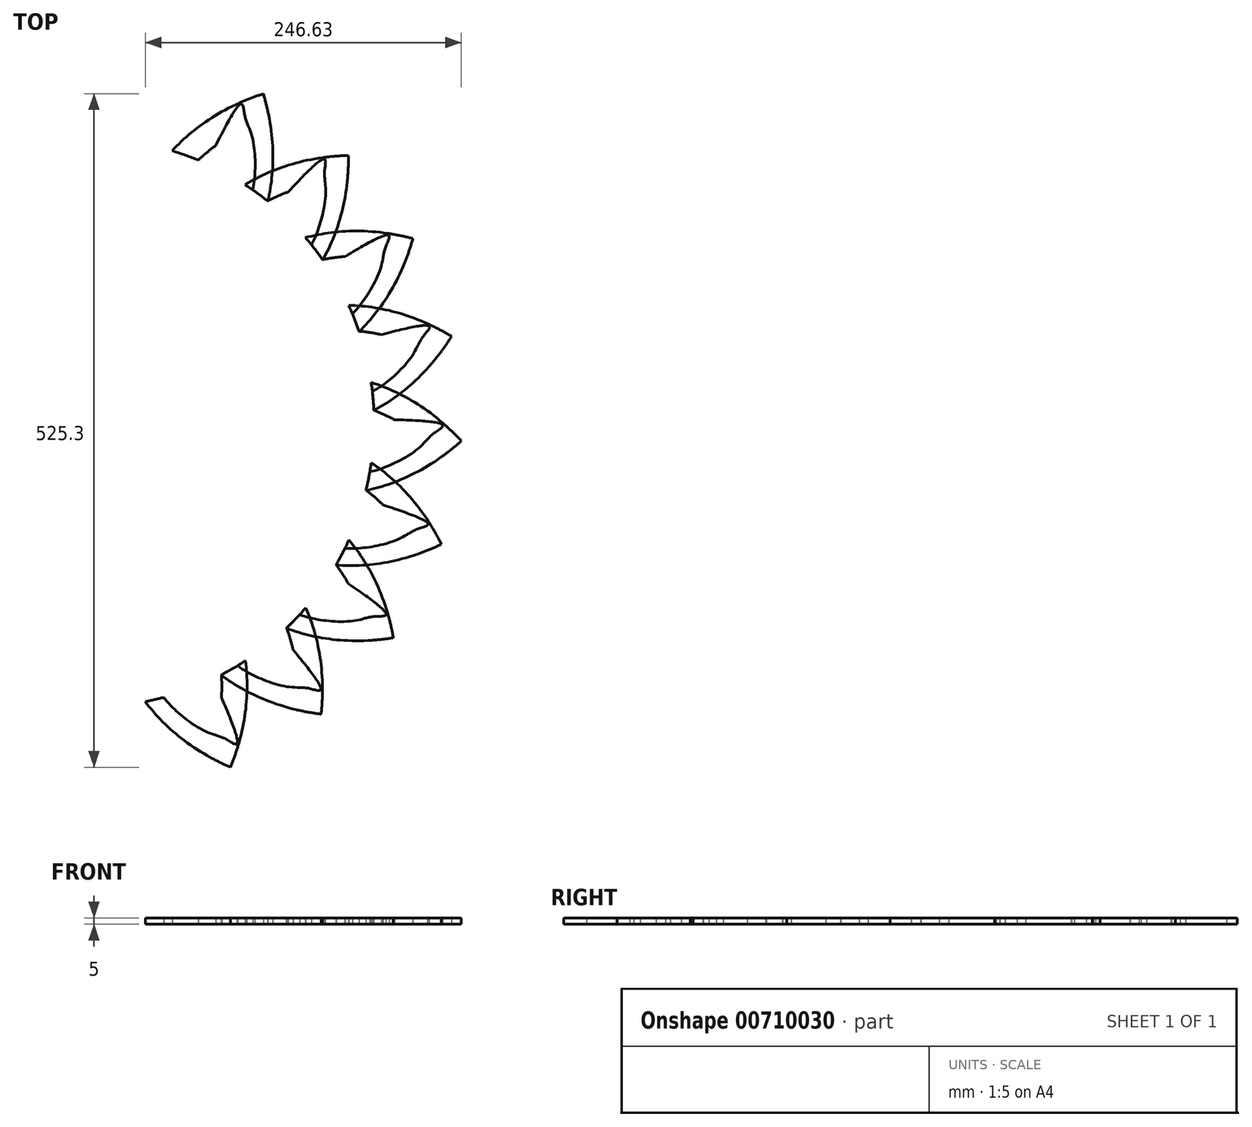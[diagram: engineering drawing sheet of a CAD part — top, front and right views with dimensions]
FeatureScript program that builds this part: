
annotation { "Feature Type Name" : "Feature", "Feature Type Description" : "" }
export const myFeature = defineFeature(function(context is Context, id is Id, definition is map)
    precondition{}
    {
        {
            var Q0;
            Q0=qCreatedBy(makeId("Top.planeOp"),FACE);
            var sketch = newSketch(context, id + "F0", { "sketchPlane" : qUnion([Q0])});
            skCircle(sketch, "E0", {"center": v(20, 0) * mm, "radius": 40 * mm});
            skArc(sketch, "E1", {"start": v(22.8, 62.44) * mm, "mid": v(-42.5, 0) * mm, "end": v(22.8, -62.44) * mm});
            skArc(sketch, "E2", {"start": v(85.64, 287.52) * mm, "mid": v(300, 0) * mm, "end": v(85.64, -287.52) * mm, "construction": true});
            skFitSpline(sketch, "E3", {"points": [v(22.8, 62.44) * mm, v(49.83, 156.63) * mm, v(155.33, 256.66) * mm], "startDerivative": vector(83.07, 317.15) * mm, "endDerivative": vector(356.58, 114.93) * mm});
            skLineSegment(sketch, "E4", {"start": v(20, 0) * mm, "end": v(155.33, 256.66) * mm, "construction": true});
            skArc(sketch, "E5", {"start": v(22.8, 62.44) * mm, "mid": v(82.5, 0) * mm, "end": v(22.8, -62.44) * mm});
            skFitSpline(sketch, "E6.0", {"points": [v(49.15, 55.29) * mm, v(53.1, 60.52) * mm, v(59.95, 69.49) * mm, v(66.7, 77.89) * mm, v(71.5, 83.5) * mm, v(74.88, 87.26) * mm, v(78.15, 90.69) * mm, v(81.35, 93.86) * mm, v(84.53, 96.85) * mm, v(87.76, 99.77) * mm, v(91.12, 102.75) * mm, v(94.15, 105.42) * mm, v(96.78, 107.76) * mm, v(99.51, 110.2) * mm, v(103.12, 113.48) * mm, v(107.66, 117.79) * mm, v(113.92, 124.05) * mm, v(121.87, 132.82) * mm, v(130.88, 144.81) * mm, v(138.68, 158.15) * mm, v(144.62, 172.78) * mm, v(148.19, 188.74) * mm, v(148.82, 206.3) * mm, v(145.77, 225.91) * mm, v(140.64, 240.62) * mm, v(137.11, 248.4) * mm, v(49.15, 55.29) * mm]});
            skFitSpline(sketch, "E7.MirrorCS", {"points": [v(69.94, 37.58) * mm, v(132.39, 113.1) * mm, v(155.33, 256.66) * mm], "startDerivative": vector(214.77, 247.7) * mm, "endDerivative": vector(-106.6, 359.16) * mm});
            skFitSpline(sketch, "E8.0", {"points": [v(54.83, 50.68) * mm, v(59.35, 55.9) * mm, v(67.68, 65.39) * mm, v(78.32, 77.37) * mm, v(87.39, 87.59) * mm, v(95.16, 96.56) * mm, v(101.96, 104.83) * mm, v(107.13, 111.63) * mm, v(111.2, 117.36) * mm, v(114.26, 121.88) * mm, v(117.4, 126.73) * mm, v(120.52, 131.83) * mm, v(123.6, 137.18) * mm, v(127.59, 144.65) * mm, v(132.25, 154.64) * mm, v(137, 167.66) * mm, v(140.58, 181.75) * mm, v(142.69, 196.98) * mm, v(143, 213.45) * mm, v(141.13, 231.31) * mm, v(138.15, 244.23) * mm, v(136.16, 250.97) * mm]});
            skFitSpline(sketch, "E8.1", {"points": [v(42.14, 57.37) * mm, v(43.89, 64.04) * mm, v(47.02, 76.28) * mm, v(50.9, 91.83) * mm, v(54.2, 105.09) * mm, v(57.22, 116.57) * mm, v(60.2, 126.85) * mm, v(62.89, 134.96) * mm, v(65.32, 141.55) * mm, v(67.32, 146.63) * mm, v(69.55, 151.96) * mm, v(71.99, 157.42) * mm, v(74.66, 162.98) * mm, v(78.58, 170.5) * mm, v(84.19, 179.98) * mm, v(92.25, 191.25) * mm, v(101.85, 202.16) * mm, v(113.22, 212.51) * mm, v(126.64, 222.07) * mm, v(142.44, 230.62) * mm, v(154.78, 235.47) * mm, v(161.46, 237.62) * mm]});
            skPoint(sketch, "E9", {"position": v(49.15, 55.29) * mm});
            skLineSegment(sketch, "E10", {"start": v(42.48, 58.66) * mm, "end": v(55.7, 51.69) * mm});
            skSolve(sketch);
        }
        {
            var Q0;
            Q0 = qSketchRegion(id + "F0", true);
            extrude(context, id + "F1", {"entities" : qUnion([Q0]), "depth" : 5 * mm, "offsetDistance" : 25 * mm});
        }
        {
            var Q0;
            Q0 = qSketchRegion(id + "F0", true);
            extrude(context, id + "F2", {"entities" : qUnion([Q0]), "operationType" : NewBodyOperationType.ADD, "depth" : 5 * mm, "offsetDistance" : 25 * mm});
        }
        {
            var Q0;
            Q0=qCreatedBy(makeId("Front.planeOp"),FACE);
            var sketch = newSketch(context, id + "F3", { "sketchPlane" : qUnion([Q0])});
            skPoint(sketch, "E11.0", {"position": v(20, 0) * mm});
            skLineSegment(sketch, "E12", {"start": v(20, 0) * mm, "end": v(20, 188.82) * mm, "construction": true});
            skSolve(sketch);
        }
        {
            var Q0;
            Q0=makeQuery(id+"F1.opExtrude","SWEPT_BODY",BODY,{"disambiguationData":[OSD([sQuery(id+"F0.wireOp",EDGE,"E0"),sQuery(id+"F0.wireOp",EDGE,"E1"),sQuery(id+"F0.wireOp",EDGE,"E3"),sQuery(id+"F0.wireOp",EDGE,"E5"),sQuery(id+"F0.wireOp",EDGE,"E7.MirrorCS"),sQuery(id+"F0.wireOp",EDGE,"E8.0"),sQuery(id+"F0.wireOp",EDGE,"E8.1"),sQuery(id+"F0.wireOp",EDGE,"JukjvdPk-2c5c-0535-gR6E-rbB6Piw5FD4A"),sQuery(id+"F0.wireOp",EDGE,"kLFv4ua1-KjQv-l3LA-NWlI-sPYLPeWq3RBU")])]});
            var Q1;
            Q1=sQuery(id+"F3.wireOp",EDGE,"E12");
            circularPattern(context, id + "F4", {"entities" : qUnion([Q0]), "axis" : qUnion([Q1]), "angle" : 130 * degree, "instanceCount" : 9, "oppositeDirection" : true, "equalSpace" : true});
        }
        {
            var Q0;
            Q0=qCreatedBy(makeId("Top.planeOp"),FACE);
            var sketch = newSketch(context, id + "F5", { "sketchPlane" : qUnion([Q0])});
            skPoint(sketch, "E13.0", {"position": v(20, 0) * mm});
            skFitSpline(sketch, "E14.0", {"points": [v(69, 38.8) * mm, v(101.6, 80.37) * mm, v(125.43, 104.66) * mm, v(174.9, 190.73) * mm, v(155.33, 256.66) * mm]});
            skFitSpline(sketch, "E15.0", {"points": [v(55.86, 49.35) * mm, v(59.67, 55.7) * mm, v(66.48, 67.2) * mm, v(74.76, 81.4) * mm, v(81.56, 93.2) * mm, v(87.34, 103.18) * mm, v(91.7, 110.48) * mm, v(95.16, 116.07) * mm, v(97.81, 120.23) * mm, v(100.6, 124.45) * mm, v(102.82, 127.74) * mm, v(104.4, 130.02) * mm, v(105.47, 131.56) * mm, v(107.4, 134.29) * mm, v(110.28, 138.27) * mm, v(113.99, 143.16) * mm, v(117.96, 148.1) * mm, v(122.22, 153.04) * mm, v(128.3, 159.58) * mm, v(136.7, 167.56) * mm, v(148.17, 176.44) * mm, v(161.22, 184.32) * mm, v(176.07, 190.88) * mm, v(193.01, 195.78) * mm, v(205.92, 197.68) * mm, v(212.84, 198.22) * mm]});
            skCircle(sketch, "E16", {"center": v(20, 0) * mm, "radius": 221.72 * mm});
            skPoint(sketch, "E17", {"position": v(158.85, 172.86) * mm});
            skSolve(sketch);
        }
        {
            var Q0;
            Q0=makeQuery(id+"F5.imprint","IMPRINT",FACE,{"disambiguationData":[TD([[makeQuery(id+"F5.imprint","IMPRINT",EDGE,{"derivedFrom":sQuery(id+"F5.wireOp",EDGE,"E16")}),1.0]])]});
            extrude(context, id + "F6", {"entities" : qUnion([Q0]), "operationType" : NewBodyOperationType.REMOVE, "depth" : 25 * mm, "offsetDistance" : 25 * mm});
        }
    });
